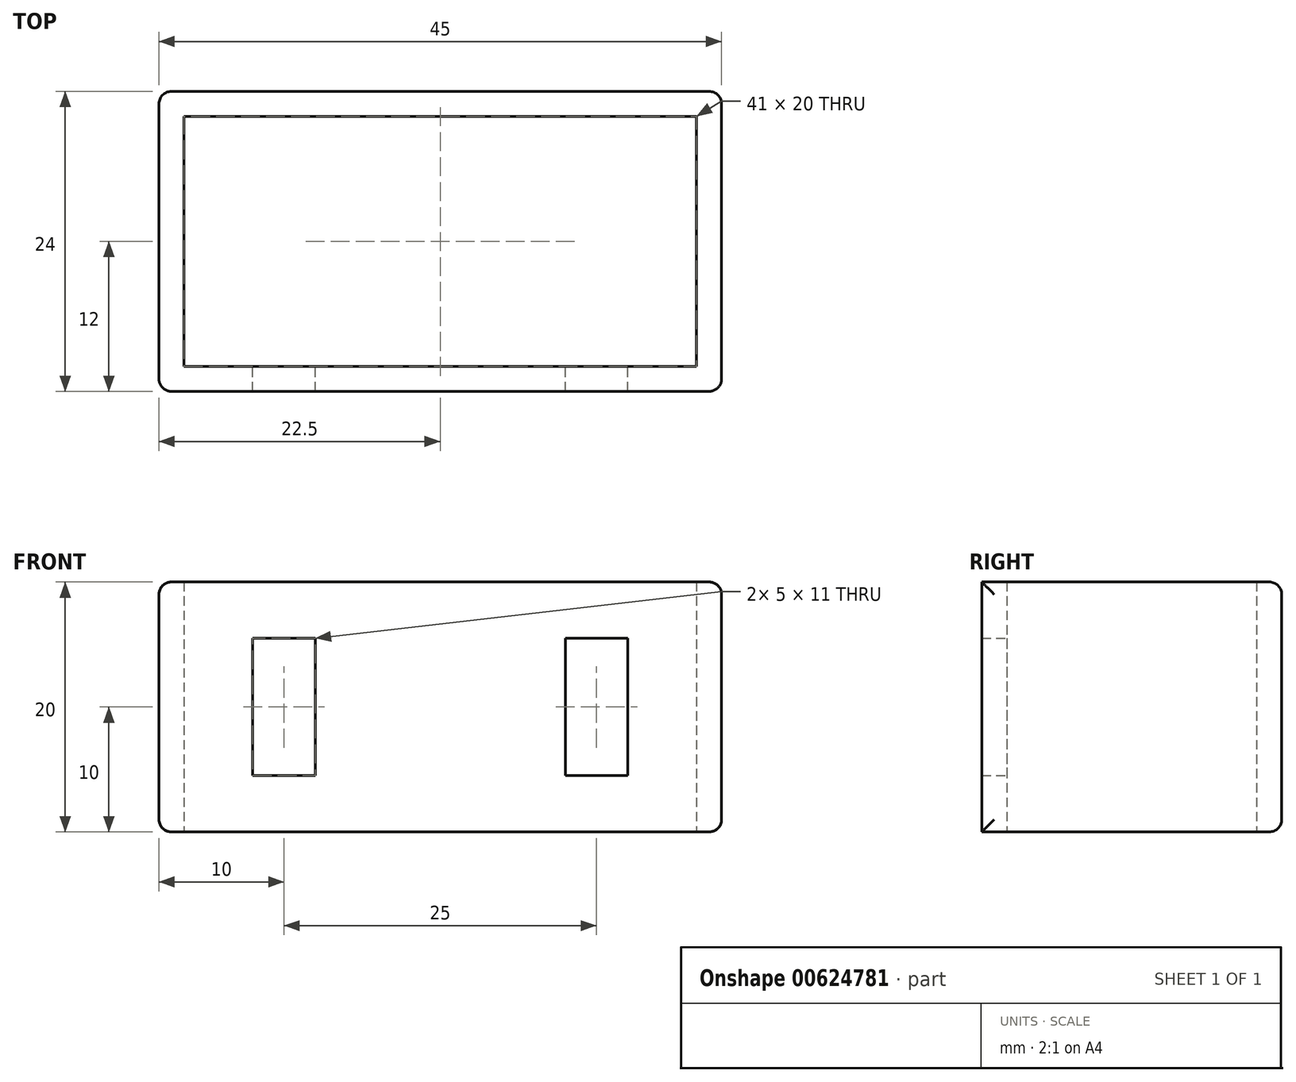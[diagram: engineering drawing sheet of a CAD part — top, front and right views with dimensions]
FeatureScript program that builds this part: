
annotation { "Feature Type Name" : "Feature", "Feature Type Description" : "" }
export const myFeature = defineFeature(function(context is Context, id is Id, definition is map)
    precondition{}
    {
        {
            var Q0;
            Q0=qCreatedBy(makeId("Front.planeOp"),FACE);
            var sketch = newSketch(context, id + "F0", { "sketchPlane" : qUnion([Q0])});
            skLineSegment(sketch, "E0.bottom", {"start": v(0, 0) * mm, "end": v(45, 0) * mm});
            skLineSegment(sketch, "E0.top", {"start": v(0, -20) * mm, "end": v(45, -20) * mm});
            skLineSegment(sketch, "E0.left", {"start": v(0, 0) * mm, "end": v(0, -20) * mm});
            skLineSegment(sketch, "E0.right", {"start": v(45, 0) * mm, "end": v(45, -20) * mm});
            skSolve(sketch);
        }
        {
            var Q0;
            Q0 = qSketchRegion(id + "F0", true);
            extrude(context, id + "F1", {"entities" : qUnion([Q0]), "depth" : 24 * mm, "offsetDistance" : 25 * mm});
        }
        {
            var Q0;
            Q0=qCreatedBy(makeId("Top.planeOp"),FACE);
            var sketch = newSketch(context, id + "F2", { "sketchPlane" : qUnion([Q0])});
            skLineSegment(sketch, "E1.bottom", {"start": v(2, -2) * mm, "end": v(43, -2) * mm});
            skLineSegment(sketch, "E1.top", {"start": v(2, -22) * mm, "end": v(43, -22) * mm});
            skLineSegment(sketch, "E1.left", {"start": v(2, -2) * mm, "end": v(2, -22) * mm});
            skLineSegment(sketch, "E1.right", {"start": v(43, -2) * mm, "end": v(43, -22) * mm});
            skSolve(sketch);
        }
        {
            var Q0;
            Q0 = qSketchRegion(id + "F2", true);
            extrude(context, id + "F3", {"entities" : qUnion([Q0]), "operationType" : NewBodyOperationType.REMOVE, "endBound" : BoundingType.SYMMETRIC, "depth" : 40 * mm, "offsetDistance" : 25 * mm});
        }
        {
            var Q0;
            Q0=makeQuery(id+"F3.boolean.opBoolean","COPY",FACE,{"derivedFrom":makeQuery(id+"F3.opExtrude","SWEPT_FACE",FACE,{"disambiguationData":[OSD([sQuery(id+"F2.wireOp",EDGE,"E1.top")])]})});
            cPlane(context, id + "F4", {"entities" : qUnion([Q0]), "cplaneType" : CPlaneType.OFFSET, "offset" : 0 * mm, "width" : 150 * mm, "height" : 150 * mm});
        }
        {
            var Q0;
            Q0=qCreatedBy(id+"F4.planeOp",FACE);
            var sketch = newSketch(context, id + "F5", { "sketchPlane" : qUnion([Q0])});
            skLineSegment(sketch, "E2.bottom", {"start": v(-12.5, -4.5) * mm, "end": v(-7.5, -4.5) * mm});
            skLineSegment(sketch, "E3.top", {"start": v(-12.5, -15.5) * mm, "end": v(-7.5, -15.5) * mm});
            skLineSegment(sketch, "E4", {"start": v(-12.5, -4.5) * mm, "end": v(-12.5, -15.5) * mm});
            skLineSegment(sketch, "E5", {"start": v(-7.5, -4.5) * mm, "end": v(-7.5, -15.5) * mm});
            skLineSegment(sketch, "E6", {"start": v(-22.5, 0) * mm, "end": v(-22.5, -20) * mm, "construction": true});
            skLineSegment(sketch, "E7", {"start": v(0, -10) * mm, "end": v(-45, -10) * mm, "construction": true});
            skPoint(sketch, "E8", {"position": v(-22.5, -10) * mm});
            skPoint(sketch, "E9", {"position": v(-20.5, 2.87) * mm});
            skLineSegment(sketch, "E10.bottom", {"start": v(-37.5, -4.5) * mm, "end": v(-32.5, -4.5) * mm});
            skLineSegment(sketch, "E11.top", {"start": v(-37.5, -15.5) * mm, "end": v(-32.5, -15.5) * mm});
            skLineSegment(sketch, "E12", {"start": v(-37.5, -4.5) * mm, "end": v(-37.5, -15.5) * mm});
            skLineSegment(sketch, "E13", {"start": v(-32.5, -4.5) * mm, "end": v(-32.5, -15.5) * mm});
            skSolve(sketch);
        }
        {
            var Q0;
            Q0 = qSketchRegion(id + "F5", true);
            extrude(context, id + "F6", {"entities" : qUnion([Q0]), "operationType" : NewBodyOperationType.REMOVE, "oppositeDirection" : true, "depth" : 5 * mm, "offsetDistance" : 25 * mm});
        }
        {
            var Q0;
            Q0=makeQuery(id+"F1.opExtrude","SWEPT_FACE",FACE,{"disambiguationData":[OSD([sQuery(id+"F0.wireOp",EDGE,"E0.right")])]});
            var Q1;
            Q1=makeQuery(id+"F1.opExtrude","CAP_FACE",FACE,{"disambiguationData":[OSD([sQuery(id+"F0.wireOp",EDGE,"E0.bottom"),sQuery(id+"F0.wireOp",EDGE,"E0.top"),sQuery(id+"F0.wireOp",EDGE,"E0.left"),sQuery(id+"F0.wireOp",EDGE,"E0.right")])],"isStart":true});
            var Q2;
            Q2=makeQuery(id+"F1.opExtrude","SWEPT_FACE",FACE,{"disambiguationData":[OSD([sQuery(id+"F0.wireOp",EDGE,"E0.left")])]});
            fillet(context, id + "F7", {"entities" : qUnion([Q0, Q1, Q2]), "radius" : 1 * mm, "tangentPropagation" : true, "allowEdgeOverflow" : false});
        }
    });
